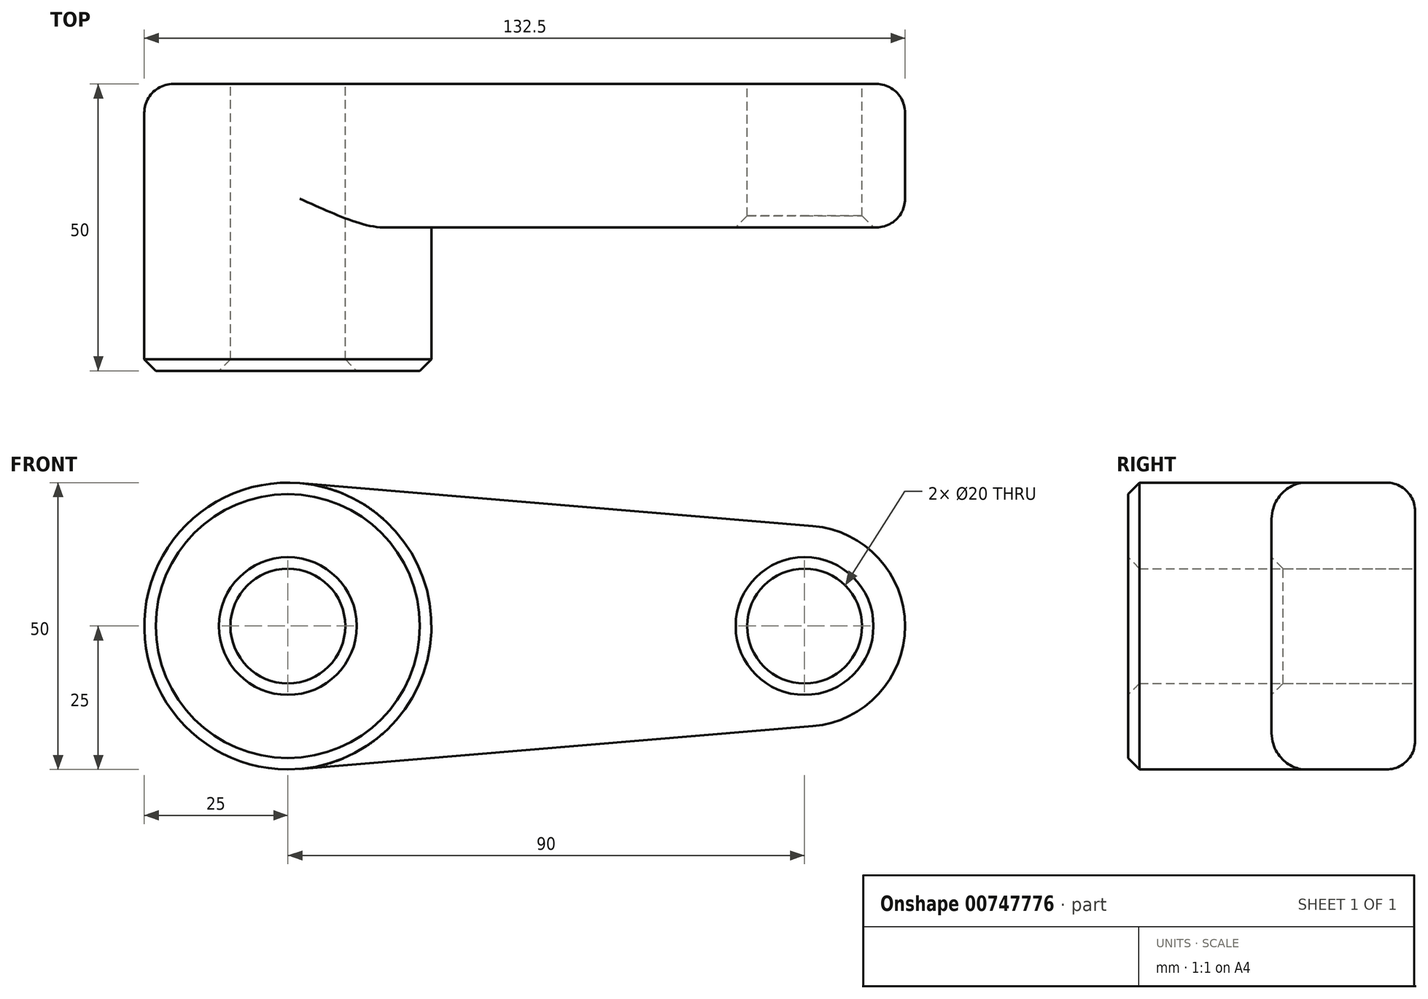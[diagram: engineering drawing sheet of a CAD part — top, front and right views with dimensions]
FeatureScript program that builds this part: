
annotation { "Feature Type Name" : "Feature", "Feature Type Description" : "" }
export const myFeature = defineFeature(function(context is Context, id is Id, definition is map)
    precondition{}
    {
        {
            var Q0;
            Q0=qCreatedBy(makeId("Front.planeOp"),FACE);
            var sketch = newSketch(context, id + "F0", { "sketchPlane" : qUnion([Q0])});
            skCircle(sketch, "E0", {"center": v(0, 0) * mm, "radius": 25 * mm});
            skCircle(sketch, "E1", {"center": v(90, 0) * mm, "radius": 17.5 * mm});
            skLineSegment(sketch, "E2", {"start": v(2.08, 24.91) * mm, "end": v(91.46, 17.44) * mm});
            skLineSegment(sketch, "E3", {"start": v(2.08, -24.91) * mm, "end": v(91.46, -17.44) * mm});
            skCircle(sketch, "E4", {"center": v(0, 0) * mm, "radius": 10 * mm});
            skCircle(sketch, "E5", {"center": v(90, 0) * mm, "radius": 10 * mm});
            skSolve(sketch);
        }
        {
            var Q0;
            Q0=qSketchRegion(id+"F0",true);
            extrude(context, id + "F1", {"entities" : qUnion([Q0]), "depth" : 25 * mm});
        }
        {
            var Q0;
            Q0=makeQuery(id+"F0.imprint","IMPRINT",FACE,{"disambiguationData":[TD([[makeQuery(id+"F0.imprint","IMPRINT",EDGE,{"derivedFrom":sQuery(id+"F0.wireOp",EDGE,"E4")}),-1.0]])]});
            extrude(context, id + "F2", {"entities" : qUnion([Q0]), "operationType" : NewBodyOperationType.ADD, "depth" : 50 * mm});
        }
        {
            var Q0;
            Q0=makeQuery(id+"F2.opExtrude","CAP_EDGE",EDGE,{"disambiguationData":[OSD([sQuery(id+"F0.wireOp",EDGE,"E0")])],"isStart":false});
            var Q1;
            Q1=makeQuery(id+"F2.opExtrude","CAP_EDGE",EDGE,{"disambiguationData":[OSD([sQuery(id+"F0.wireOp",EDGE,"E4")])],"isStart":false});
            var Q2;
            Q2=makeQuery(id+"F1.opExtrude","CAP_EDGE",EDGE,{"disambiguationData":[OSD([sQuery(id+"F0.wireOp",EDGE,"E5")])],"isStart":false});
            chamfer(context, id + "F3", {"entities" : qUnion([Q0, Q1, Q2]), "width" : 2 * mm, "tangentPropagation" : true});
        }
        {
            var Q0;
            Q0=makeQuery(id+"F1.opExtrude","CAP_EDGE",EDGE,{"disambiguationData":[OSD([sQuery(id+"F0.wireOp",EDGE,"E2")])],"isStart":false});
            var Q1;
            Q1=makeQuery(id+"F1.opExtrude","CAP_EDGE",EDGE,{"disambiguationData":[OSD([sQuery(id+"F0.wireOp",EDGE,"E3")])],"isStart":true});
            fillet(context, id + "F4", {"entities" : qUnion([Q0, Q1]), "radius" : 5 * mm, "tangentPropagation" : true, "allowEdgeOverflow" : false});
        }
    });
